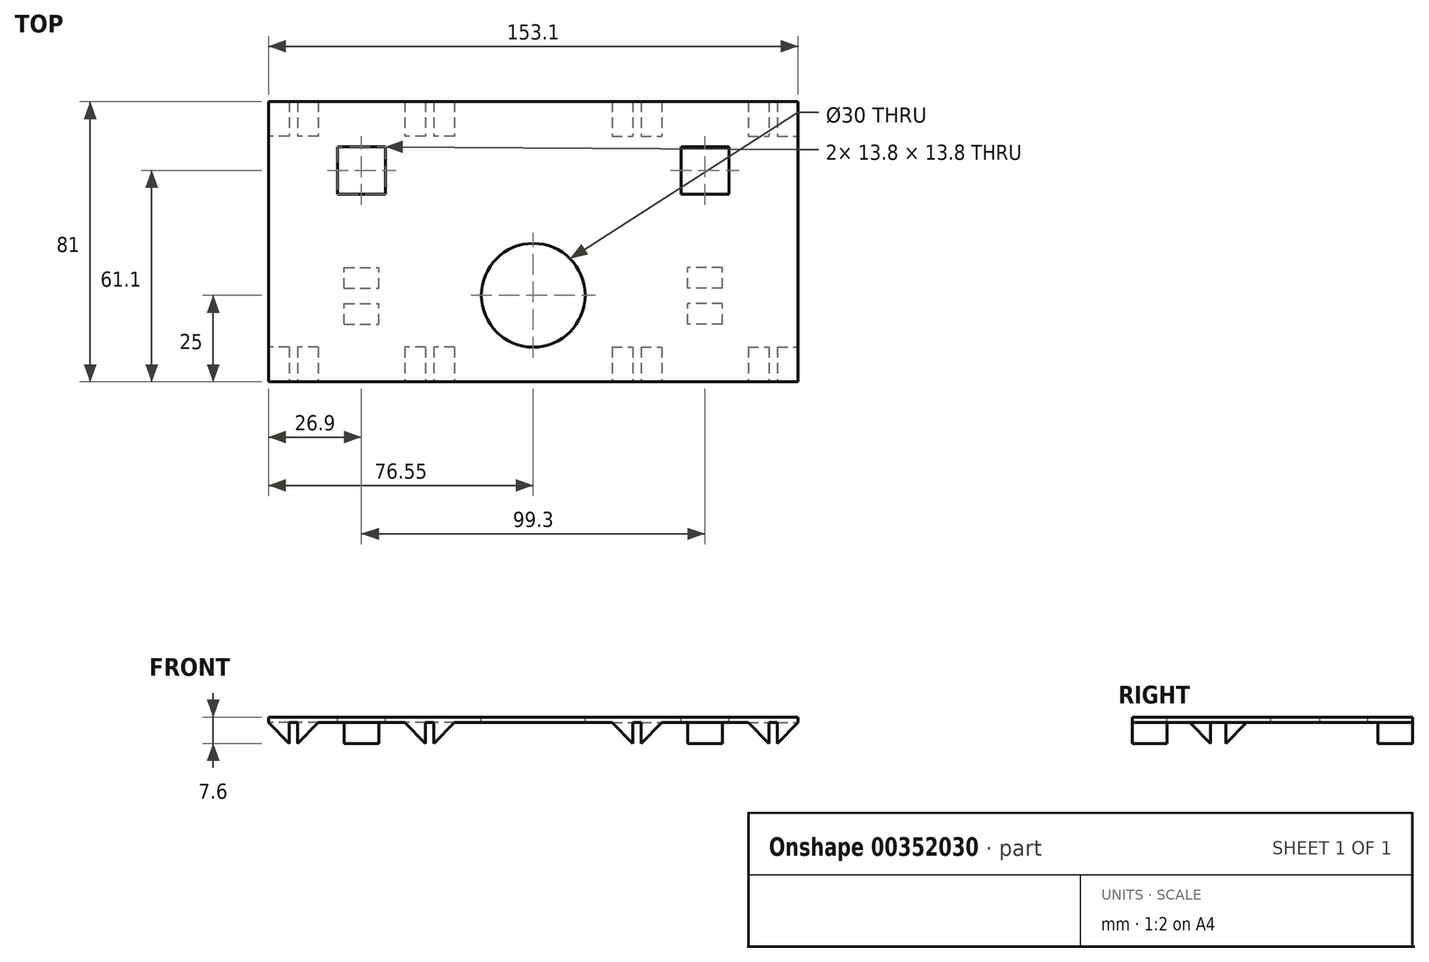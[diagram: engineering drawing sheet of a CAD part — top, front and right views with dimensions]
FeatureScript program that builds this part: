
annotation { "Feature Type Name" : "Feature", "Feature Type Description" : "" }
export const myFeature = defineFeature(function(context is Context, id is Id, definition is map)
    precondition{}
    {
        {
            var Q0;
            Q0=qCreatedBy(makeId("Front.planeOp"),FACE);
            cPlane(context, id + "F0", {"entities" : qUnion([Q0]), "cplaneType" : CPlaneType.OFFSET, "offset" : 40.5 * mm, "width" : 150 * mm, "height" : 150 * mm});
        }
        {
            var Q0;
            Q0=qCreatedBy(id+"F0.planeOp",FACE);
            var sketch = newSketch(context, id + "F1", { "sketchPlane" : qUnion([Q0])});
            skLineSegment(sketch, "E0", {"start": v(76.55, 1.6) * mm, "end": v(76.55, 0) * mm});
            skLineSegment(sketch, "E1", {"start": v(76.55, 0) * mm, "end": v(-76.55, 0) * mm});
            skLineSegment(sketch, "E2", {"start": v(-76.55, 0) * mm, "end": v(-76.55, 1.6) * mm});
            skLineSegment(sketch, "E3", {"start": v(-76.55, 1.6) * mm, "end": v(76.55, 1.6) * mm});
            skLineSegment(sketch, "E4", {"start": v(-70.55, -6) * mm, "end": v(-70.55, 0) * mm});
            skLineSegment(sketch, "E5", {"start": v(-76.55, 0) * mm, "end": v(-70.55, 0) * mm});
            skLineSegment(sketch, "E6", {"start": v(-68.15, 0) * mm, "end": v(-68.15, -6) * mm});
            skLineSegment(sketch, "E7", {"start": v(-62.15, 0) * mm, "end": v(-68.15, 0) * mm});
            skLineSegment(sketch, "E8", {"start": v(-28.75, 0) * mm, "end": v(-28.75, -6) * mm});
            skLineSegment(sketch, "E9", {"start": v(-22.75, 0) * mm, "end": v(-28.75, 0) * mm});
            skLineSegment(sketch, "E10", {"start": v(-31.15, 0) * mm, "end": v(-31.15, -6) * mm});
            skLineSegment(sketch, "E11", {"start": v(-37.15, 0) * mm, "end": v(-31.15, 0) * mm});
            skLineSegment(sketch, "E12.MirrorCS", {"start": v(22.75, -10) * mm, "end": v(22.75, 0) * mm});
            skLineSegment(sketch, "E13.MirrorCS", {"start": v(28.75, 0) * mm, "end": v(28.75, -6) * mm});
            skLineSegment(sketch, "E14.MirrorCS", {"start": v(37.15, -10) * mm, "end": v(37.15, 0) * mm});
            skLineSegment(sketch, "E15.MirrorCS", {"start": v(31.15, 0) * mm, "end": v(31.15, -6) * mm});
            skLineSegment(sketch, "E16.MirrorCS", {"start": v(31.15, -6) * mm, "end": v(32.75, -6) * mm});
            skLineSegment(sketch, "E17.MirrorCS", {"start": v(37.15, 0) * mm, "end": v(31.15, 0) * mm});
            skLineSegment(sketch, "E18.MirrorCS", {"start": v(68.15, 0) * mm, "end": v(68.15, -6) * mm});
            skLineSegment(sketch, "E19.MirrorCS", {"start": v(62.15, -10) * mm, "end": v(62.15, 0) * mm});
            skLineSegment(sketch, "E20.MirrorCS", {"start": v(62.15, 0) * mm, "end": v(68.15, 0) * mm});
            skLineSegment(sketch, "E21.MirrorCS", {"start": v(70.55, -6) * mm, "end": v(70.55, 0) * mm});
            skLineSegment(sketch, "E22.MirrorCS", {"start": v(76.55, 0) * mm, "end": v(70.55, 0) * mm});
            skLineSegment(sketch, "E23.MirrorCS", {"start": v(76.55, 0) * mm, "end": v(76.55, -10) * mm});
            skLineSegment(sketch, "E24.MirrorCS", {"start": v(72.15, -6) * mm, "end": v(70.55, -6) * mm});
            skLineSegment(sketch, "E25.MirrorCS", {"start": v(68.15, -6) * mm, "end": v(66.55, -6) * mm});
            skLineSegment(sketch, "E26.MirrorCS", {"start": v(28.75, -6) * mm, "end": v(27.15, -6) * mm});
            skLineSegment(sketch, "E27", {"start": v(-28.75, 0) * mm, "end": v(-22.75, 0) * mm});
            skLineSegment(sketch, "E28", {"start": v(22.75, 0) * mm, "end": v(28.75, 0) * mm});
            skLineSegment(sketch, "E29", {"start": v(-70.55, -6) * mm, "end": v(-76.55, 0) * mm});
            skLineSegment(sketch, "E30", {"start": v(-62.15, 0) * mm, "end": v(-68.15, -6) * mm});
            skLineSegment(sketch, "E31", {"start": v(-37.15, 0) * mm, "end": v(-31.15, -6) * mm});
            skLineSegment(sketch, "E32", {"start": v(-22.75, 0) * mm, "end": v(-28.75, -6) * mm});
            skSolve(sketch);
        }
        {
            var Q0;
            Q0=makeQuery(id+"F1.imprint","IMPRINT",FACE,{"disambiguationData":[TD([[makeQuery(id+"F1.imprint","IMPRINT",EDGE,{"derivedFrom":sQuery(id+"F1.wireOp",EDGE,"E0")}),-1.0]])]});
            extrude(context, id + "F2", {"entities" : qUnion([Q0]), "oppositeDirection" : true, "depth" : 81 * mm});
        }
        {
            var Q0;
            Q0=makeQuery(id+"F1.imprint","IMPRINT",FACE,{"disambiguationData":[TD([[makeQuery(id+"F1.imprint","IMPRINT",EDGE,{"derivedFrom":sQuery(id+"F1.wireOp",EDGE,"FF6IQarz-4mcM-jOca-ocC3-CsUcrpMwuvCt")}),1.0]])]});
            var Q1;
            Q1=makeQuery(id+"F1.imprint","IMPRINT",FACE,{"disambiguationData":[TD([[makeQuery(id+"F1.imprint","IMPRINT",EDGE,{"derivedFrom":sQuery(id+"F1.wireOp",EDGE,"E6")}),1.0]])]});
            var Q2;
            Q2=makeQuery(id+"F1.imprint","IMPRINT",FACE,{"disambiguationData":[TD([[makeQuery(id+"F1.imprint","IMPRINT",EDGE,{"derivedFrom":sQuery(id+"F1.wireOp",EDGE,"E10")}),-1.0]])]});
            var Q3;
            Q3=makeQuery(id+"F1.imprint","IMPRINT",FACE,{"disambiguationData":[TD([[makeQuery(id+"F1.imprint","IMPRINT",EDGE,{"derivedFrom":sQuery(id+"F1.wireOp",EDGE,"E8")}),1.0]])]});
            var Q4;
            Q4=makeQuery(id+"F1.imprint","IMPRINT",FACE,{"disambiguationData":[TD([[makeQuery(id+"F1.imprint","IMPRINT",EDGE,{"derivedFrom":sQuery(id+"F1.wireOp",EDGE,"E12.MirrorCS")}),-1.0]])]});
            var Q5;
            Q5=makeQuery(id+"F1.imprint","IMPRINT",FACE,{"disambiguationData":[TD([[makeQuery(id+"F1.imprint","IMPRINT",EDGE,{"derivedFrom":sQuery(id+"F1.wireOp",EDGE,"E14.MirrorCS")}),1.0]])]});
            var Q6;
            Q6=makeQuery(id+"F1.imprint","IMPRINT",FACE,{"disambiguationData":[TD([[makeQuery(id+"F1.imprint","IMPRINT",EDGE,{"derivedFrom":sQuery(id+"F1.wireOp",EDGE,"E18.MirrorCS")}),-1.0]])]});
            var Q7;
            Q7=makeQuery(id+"F1.imprint","IMPRINT",FACE,{"disambiguationData":[TD([[makeQuery(id+"F1.imprint","IMPRINT",EDGE,{"derivedFrom":sQuery(id+"F1.wireOp",EDGE,"E21.MirrorCS")}),-1.0]])]});
            var Q8;
            Q8=makeQuery(id+"F1.imprint","IMPRINT",FACE,{"disambiguationData":[TD([[makeQuery(id+"F1.imprint","IMPRINT",EDGE,{"derivedFrom":sQuery(id+"F1.wireOp",EDGE,"E4")}),1.0]])]});
            extrude(context, id + "F3", {"entities" : qUnion([Q0, Q1, Q2, Q3, Q4, Q5, Q6, Q7, Q8]), "operationType" : NewBodyOperationType.ADD, "oppositeDirection" : true, "depth" : 10 * mm});
        }
        {
            var Q0;
            Q0=makeQuery(id+"F1.imprint","IMPRINT",FACE,{"disambiguationData":[TD([[makeQuery(id+"F1.imprint","IMPRINT",EDGE,{"derivedFrom":sQuery(id+"F1.wireOp",EDGE,"FF6IQarz-4mcM-jOca-ocC3-CsUcrpMwuvCt")}),1.0]])]});
            var Q1;
            Q1=makeQuery(id+"F1.imprint","IMPRINT",FACE,{"disambiguationData":[TD([[makeQuery(id+"F1.imprint","IMPRINT",EDGE,{"derivedFrom":sQuery(id+"F1.wireOp",EDGE,"E6")}),1.0]])]});
            var Q2;
            Q2=makeQuery(id+"F1.imprint","IMPRINT",FACE,{"disambiguationData":[TD([[makeQuery(id+"F1.imprint","IMPRINT",EDGE,{"derivedFrom":sQuery(id+"F1.wireOp",EDGE,"E10")}),-1.0]])]});
            var Q3;
            Q3=makeQuery(id+"F1.imprint","IMPRINT",FACE,{"disambiguationData":[TD([[makeQuery(id+"F1.imprint","IMPRINT",EDGE,{"derivedFrom":sQuery(id+"F1.wireOp",EDGE,"E8")}),1.0]])]});
            var Q4;
            Q4=makeQuery(id+"F1.imprint","IMPRINT",FACE,{"disambiguationData":[TD([[makeQuery(id+"F1.imprint","IMPRINT",EDGE,{"derivedFrom":sQuery(id+"F1.wireOp",EDGE,"E14.MirrorCS")}),1.0]])]});
            var Q5;
            Q5=makeQuery(id+"F1.imprint","IMPRINT",FACE,{"disambiguationData":[TD([[makeQuery(id+"F1.imprint","IMPRINT",EDGE,{"derivedFrom":sQuery(id+"F1.wireOp",EDGE,"E12.MirrorCS")}),-1.0]])]});
            var Q6;
            Q6=makeQuery(id+"F1.imprint","IMPRINT",FACE,{"disambiguationData":[TD([[makeQuery(id+"F1.imprint","IMPRINT",EDGE,{"derivedFrom":sQuery(id+"F1.wireOp",EDGE,"E18.MirrorCS")}),-1.0]])]});
            var Q7;
            Q7=makeQuery(id+"F1.imprint","IMPRINT",FACE,{"disambiguationData":[TD([[makeQuery(id+"F1.imprint","IMPRINT",EDGE,{"derivedFrom":sQuery(id+"F1.wireOp",EDGE,"E21.MirrorCS")}),-1.0]])]});
            var Q8;
            Q8=makeQuery(id+"F1.imprint","IMPRINT",FACE,{"disambiguationData":[TD([[makeQuery(id+"F1.imprint","IMPRINT",EDGE,{"derivedFrom":sQuery(id+"F1.wireOp",EDGE,"E4")}),1.0]])]});
            extrude(context, id + "F4", {"entities" : qUnion([Q0, Q1, Q2, Q3, Q4, Q5, Q6, Q7, Q8]), "operationType" : NewBodyOperationType.ADD, "oppositeDirection" : true, "depth" : 81 * mm, "hasSecondDirection" : true, "secondDirectionOppositeDirection" : true, "secondDirectionDepth" : 71 * mm});
        }
        {
            var Q0;
            Q0=qCreatedBy(makeId("Right.planeOp"),FACE);
            cPlane(context, id + "F5", {"entities" : qUnion([Q0]), "cplaneType" : CPlaneType.OFFSET, "offset" : 49.65 * mm, "oppositeDirection" : true, "width" : 150 * mm, "height" : 150 * mm});
        }
        {
            var Q0;
            Q0=qCreatedBy(id+"F5.planeOp",FACE);
            var sketch = newSketch(context, id + "F6", { "sketchPlane" : qUnion([Q0])});
            skLineSegment(sketch, "E33", {"start": v(-13.5, -6) * mm, "end": v(-13.5, 0) * mm});
            skLineSegment(sketch, "E34", {"start": v(-13.5, 0) * mm, "end": v(-7.5, 0) * mm});
            skLineSegment(sketch, "E35", {"start": v(-17.9, 0) * mm, "end": v(-17.9, -6) * mm});
            skLineSegment(sketch, "E36", {"start": v(-23.9, 0) * mm, "end": v(-17.9, 0) * mm});
            skLineSegment(sketch, "E37", {"start": v(-23.9, 0) * mm, "end": v(-17.9, -6) * mm});
            skLineSegment(sketch, "E38", {"start": v(-7.5, 0) * mm, "end": v(-13.5, -6) * mm});
            skSolve(sketch);
        }
        {
            var Q0;
            Q0=qSketchRegion(id+"F6",true);
            extrude(context, id + "F7", {"entities" : qUnion([Q0]), "operationType" : NewBodyOperationType.ADD, "endBound" : BoundingType.SYMMETRIC, "oppositeDirection" : true, "depth" : 10 * mm});
        }
        {
            var Q0;
            Q0=makeQuery(id+"F2.opExtrude","SWEPT_BODY",BODY,{"disambiguationData":[OSD([sQuery(id+"F1.wireOp",EDGE,"E0"),sQuery(id+"F1.wireOp",EDGE,"E1"),sQuery(id+"F1.wireOp",EDGE,"E2"),sQuery(id+"F1.wireOp",EDGE,"E3"),sQuery(id+"F1.wireOp",EDGE,"E5"),sQuery(id+"F1.wireOp",EDGE,"E7"),sQuery(id+"F1.wireOp",EDGE,"E11"),sQuery(id+"F1.wireOp",EDGE,"E17.MirrorCS"),sQuery(id+"F1.wireOp",EDGE,"E20.MirrorCS"),sQuery(id+"F1.wireOp",EDGE,"E22.MirrorCS"),sQuery(id+"F1.wireOp",EDGE,"E27"),sQuery(id+"F1.wireOp",EDGE,"E28")])]});
            var Q1;
            Q1=qCreatedBy(makeId("Right.planeOp"),FACE);
            mirror(context, id + "F8", {"operationType" : NewBodyOperationType.ADD, "entities" : qUnion([Q0]), "mirrorPlane" : qUnion([Q1])});
        }
        {
            var Q0;
            Q0=makeQuery(id+"F2.opExtrude","SWEPT_FACE",FACE,{"disambiguationData":[OSD([sQuery(id+"F1.wireOp",EDGE,"E3")])]});
            var sketch = newSketch(context, id + "F9", { "sketchPlane" : qUnion([Q0])});
            skCircle(sketch, "E39", {"center": v(0, -15.5) * mm, "radius": 15 * mm});
            skSolve(sketch);
        }
        {
            var Q0;
            Q0=qSketchRegion(id+"F9",true);
            extrude(context, id + "F10", {"entities" : qUnion([Q0]), "operationType" : NewBodyOperationType.REMOVE, "oppositeDirection" : true, "depth" : 1.6 * mm});
        }
        {
            var Q0;
            Q0=makeQuery(id+"F2.opExtrude","SWEPT_FACE",FACE,{"disambiguationData":[OSD([sQuery(id+"F1.wireOp",EDGE,"E3")])]});
            var sketch = newSketch(context, id + "F11", { "sketchPlane" : qUnion([Q0])});
            skLineSegment(sketch, "E40.bottom", {"start": v(-56.55, 27.5) * mm, "end": v(-42.75, 27.5) * mm});
            skLineSegment(sketch, "E40.top", {"start": v(-56.55, 13.7) * mm, "end": v(-42.75, 13.7) * mm});
            skLineSegment(sketch, "E40.left", {"start": v(-56.55, 27.5) * mm, "end": v(-56.55, 13.7) * mm});
            skLineSegment(sketch, "E40.right", {"start": v(-42.75, 27.5) * mm, "end": v(-42.75, 13.7) * mm});
            skLineSegment(sketch, "E41.MirrorCS", {"start": v(56.55, 27.5) * mm, "end": v(42.75, 27.5) * mm});
            skLineSegment(sketch, "E42.MirrorCS", {"start": v(42.75, 27.5) * mm, "end": v(42.75, 13.7) * mm});
            skLineSegment(sketch, "E43.MirrorCS", {"start": v(56.55, 13.7) * mm, "end": v(42.75, 13.7) * mm});
            skLineSegment(sketch, "E44.MirrorCS", {"start": v(56.55, 27.5) * mm, "end": v(56.55, 13.7) * mm});
            skSolve(sketch);
        }
        {
            var Q0;
            Q0=qSketchRegion(id+"F11",true);
            extrude(context, id + "F12", {"entities" : qUnion([Q0]), "operationType" : NewBodyOperationType.REMOVE, "oppositeDirection" : true, "depth" : 1.6 * mm});
        }
    });
